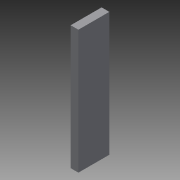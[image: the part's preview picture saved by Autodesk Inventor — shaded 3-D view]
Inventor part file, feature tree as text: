
AUTODESK INVENTOR PART (.ipt)
format: ipt  version: 2013 (Build 170138000, 138)  size: 64,512 bytes
history: native  units: in
note: dims shown in document units (in); Inventor stores cm internally (conversion verified against a paired STEP export)
features: extrude x1, sketch x1
ambient origin geometry x8: Origin, YZ Plane, XZ Plane, XY Plane, X Axis, Y Axis, Z Axis, Center Point
bodies: Solid1 (feature_tree)
feature tree (2):
  extrude  "Extrusion1"  Depth=1.0in
  sketch  "Sketch1"  dims[d0=4.0in d1=1.0in d2=0.25in d3=0.0in]
